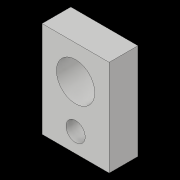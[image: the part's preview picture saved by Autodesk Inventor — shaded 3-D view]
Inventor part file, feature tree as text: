
AUTODESK INVENTOR PART (.ipt)
format: ipt  version: 2017 (Build 210142000, 142)  size: 112,640 bytes
history: native  units: in
note: dims shown in document units (in); Inventor stores cm internally (conversion verified against a paired STEP export)
features: sketch x3, extrude x2, hole x1
ambient origin geometry x8: Origin, YZ Plane, XZ Plane, XY Plane, X Axis, Y Axis, Z Axis, Center Point
bodies: Solid1 (feature_tree)
feature tree (6):
  extrude  "Extrusion1"  Depth=0.5in
  hole  "Hole1"  [1 undecoded]
  extrude  "Extrusion2"  Depth=0.1in
  sketch  "Sketch1"  dims[d0=0.35in d1=0.5in]
  sketch  "Sketch2"  dims[d2=0.15in d3=0.0in d4=0.25in]
  sketch  "Sketch3"  dims[d5=0.175in d6=0.1748in d7=0.2in d8=0.5in d9=0.375in d10=0.25in d11=0.5635in d12=0.75in d13=0.0in d14=0.1in d15=0.1in d16=0.175in d17=1.0in d18=0.0in]
note: 1 required parameter value undecoded (feature->parameter linkage not recoverable at this tier; creation-order binding heuristic only, values carry confidence <= 0.55)
